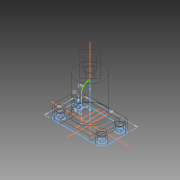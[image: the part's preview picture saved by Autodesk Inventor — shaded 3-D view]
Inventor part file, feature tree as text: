
AUTODESK INVENTOR PART (.ipt)
format: ipt  version: 2011 SP2 (Build 150309200, 309)  size: 167,936 bytes
history: native  units: mm
features: sketch x5, extrude x5, hole x2, fillet x1
ambient origin geometry x8: Origin, YZ Plane, XZ Plane, XY Plane, X Axis, Y Axis, Z Axis, Center Point
bodies: Solid1 (feature_tree)
feature tree (13):
  sketch  "Sketch1"  dims[d3=50.0mm d4=90.0mm]
  extrude  "Extrusion1"  Depth=90.0mm
  extrude  "Extrusion2"  Depth=5.0mm
  extrude  "Extrusion3"  Depth=15.0mm TaperAngle=0.0deg
  extrude  "Extrusion4"  Depth=7.0mm
  extrude  "Extrusion5"  Depth=50.0mm TaperAngle=0.0deg
  fillet  "Fillet1"  Radius=22.5mm
  hole  "Hole1"  [1 undecoded]
  hole  "Hole2"  [1 undecoded]
  sketch  "Sketch5"  dims[d21=50.0mm d22=50.0mm d23=0.0mm d24=22.5mm d27=60.0mm d28=0.0mm d30=25.0mm d31=25.0mm d32=25.0mm d33=25.0mm d34=25.0mm d35=0.0mm d36=2.0mm d37=12.5mm d38=12.5mm d39=16.0mm d40=6.0mm d41=4.0mm d42=2.0mm d43=90.0deg d44=20.0mm d45=0.0mm d46=10.0mm d47=10.0mm d48=12.0mm d49=6.0mm d50=4.0mm d51=2.0mm d52=90.0deg d53=10.0mm d54=20.594885mm d57=15.0mm]
  sketch  "Sketch2"  dims[d6=10.0mm d10=5.0mm]
  sketch  "Sketch3"  dims[d14=6.0mm d15=15.0mm d16=0.0mm]
  sketch  "Sketch4"  dims[d17=10.0mm d18=0.0mm d20=7.0mm]
note: 2 required parameter values undecoded (feature->parameter linkage not recoverable at this tier; creation-order binding heuristic only, values carry confidence <= 0.55)
